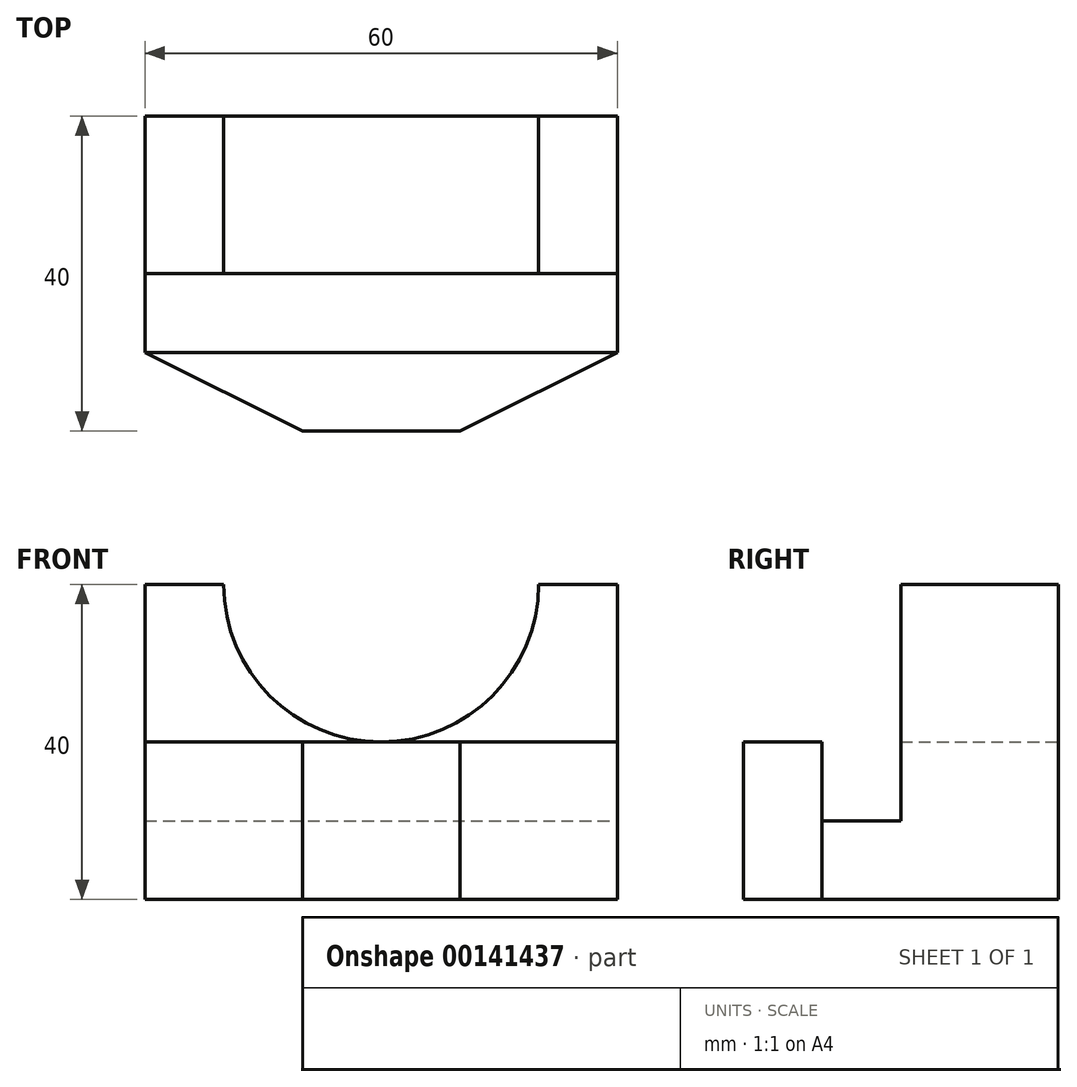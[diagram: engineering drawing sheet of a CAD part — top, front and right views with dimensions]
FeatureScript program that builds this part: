
annotation { "Feature Type Name" : "Feature", "Feature Type Description" : "" }
export const myFeature = defineFeature(function(context is Context, id is Id, definition is map)
    precondition{}
    {
        {
            var Q0;
            Q0=qCreatedBy(makeId("Front.planeOp"),FACE);
            var sketch = newSketch(context, id + "F0", { "sketchPlane" : qUnion([Q0])});
            skLineSegment(sketch, "E0", {"start": v(0, 0) * mm, "end": v(-30, 0) * mm});
            skLineSegment(sketch, "E1", {"start": v(-30, 0) * mm, "end": v(-30, 40) * mm});
            skLineSegment(sketch, "E2", {"start": v(-30, 40) * mm, "end": v(-20, 40) * mm});
            skArc(sketch, "E3", {"start": v(-20, 40) * mm, "mid": v(-14.14, 25.86) * mm, "end": v(0, 20) * mm});
            skLineSegment(sketch, "E4", {"start": v(0, 0) * mm, "end": v(0, 55.91) * mm, "construction": true});
            skPoint(sketch, "E5.orphan", {"position": v(20, 40) * mm});
            skLineSegment(sketch, "E6.MirrorCS", {"start": v(30, 40) * mm, "end": v(20, 40) * mm});
            skArc(sketch, "E7.MirrorCS", {"start": v(20, 40) * mm, "mid": v(14.14, 25.86) * mm, "end": v(0, 20) * mm});
            skLineSegment(sketch, "E8.MirrorCS", {"start": v(0, 0) * mm, "end": v(30, 0) * mm});
            skLineSegment(sketch, "E9.MirrorCS", {"start": v(30, 0) * mm, "end": v(30, 40) * mm});
            skPoint(sketch, "E10.MirrorP", {"position": v(-20, 40) * mm});
            skSolve(sketch);
        }
        {
            var Q0;
            Q0 = qSketchRegion(id + "F0", true);
            extrude(context, id + "F1", {"entities" : qUnion([Q0]), "depth" : 20 * mm});
        }
        {
            var Q0;
            Q0=makeQuery(id+"F1.opExtrude","CAP_FACE",FACE,{"disambiguationData":[OSD([sQuery(id+"F0.wireOp",EDGE,"E0"),sQuery(id+"F0.wireOp",EDGE,"E1"),sQuery(id+"F0.wireOp",EDGE,"E2"),sQuery(id+"F0.wireOp",EDGE,"E3"),sQuery(id+"F0.wireOp",EDGE,"E6.MirrorCS"),sQuery(id+"F0.wireOp",EDGE,"E7.MirrorCS"),sQuery(id+"F0.wireOp",EDGE,"E8.MirrorCS"),sQuery(id+"F0.wireOp",EDGE,"E9.MirrorCS")])],"isStart":false});
            var sketch = newSketch(context, id + "F2", { "sketchPlane" : qUnion([Q0])});
            skLineSegment(sketch, "E11.bottom", {"start": v(-30, 0) * mm, "end": v(30, 0) * mm});
            skLineSegment(sketch, "E11.top", {"start": v(-30, 10) * mm, "end": v(30, 10) * mm});
            skLineSegment(sketch, "E11.left", {"start": v(-30, 0) * mm, "end": v(-30, 10) * mm});
            skLineSegment(sketch, "E11.right", {"start": v(30, 0) * mm, "end": v(30, 10) * mm});
            skSolve(sketch);
        }
        {
            var Q0;
            Q0 = qSketchRegion(id + "F2", true);
            extrude(context, id + "F3", {"entities" : qUnion([Q0]), "operationType" : NewBodyOperationType.ADD, "depth" : 10 * mm});
        }
        {
            var Q0;
            Q0=makeQuery(id+"F3.boolean.opBoolean","MERGE",FACE,{"derivedFrom":[makeQuery(id+"F1.opExtrude","SWEPT_FACE",FACE,{"disambiguationData":[OSD([sQuery(id+"F0.wireOp",EDGE,"E0"),sQuery(id+"F0.wireOp",EDGE,"E8.MirrorCS")])]}),makeQuery(id+"F3.opExtrude","SWEPT_FACE",FACE,{"disambiguationData":[OSD([sQuery(id+"F2.wireOp",EDGE,"E11.bottom")])]})]});
            var sketch = newSketch(context, id + "F4", { "sketchPlane" : qUnion([Q0])});
            skLineSegment(sketch, "E12", {"start": v(-30, 30) * mm, "end": v(-10, 40) * mm});
            skLineSegment(sketch, "E13", {"start": v(-10, 40) * mm, "end": v(0, 40) * mm});
            skLineSegment(sketch, "E14", {"start": v(0, 30) * mm, "end": v(-30, 30) * mm});
            skLineSegment(sketch, "E15.MirrorCS", {"start": v(30, 30) * mm, "end": v(10, 40) * mm});
            skLineSegment(sketch, "E16.MirrorCS", {"start": v(10, 40) * mm, "end": v(0, 40) * mm});
            skLineSegment(sketch, "E17", {"start": v(0, 30) * mm, "end": v(30, 30) * mm});
            skSolve(sketch);
        }
        {
            var Q0;
            Q0 = qSketchRegion(id + "F4", true);
            extrude(context, id + "F5", {"entities" : qUnion([Q0]), "operationType" : NewBodyOperationType.ADD, "oppositeDirection" : true, "depth" : 20 * mm});
        }
    });
